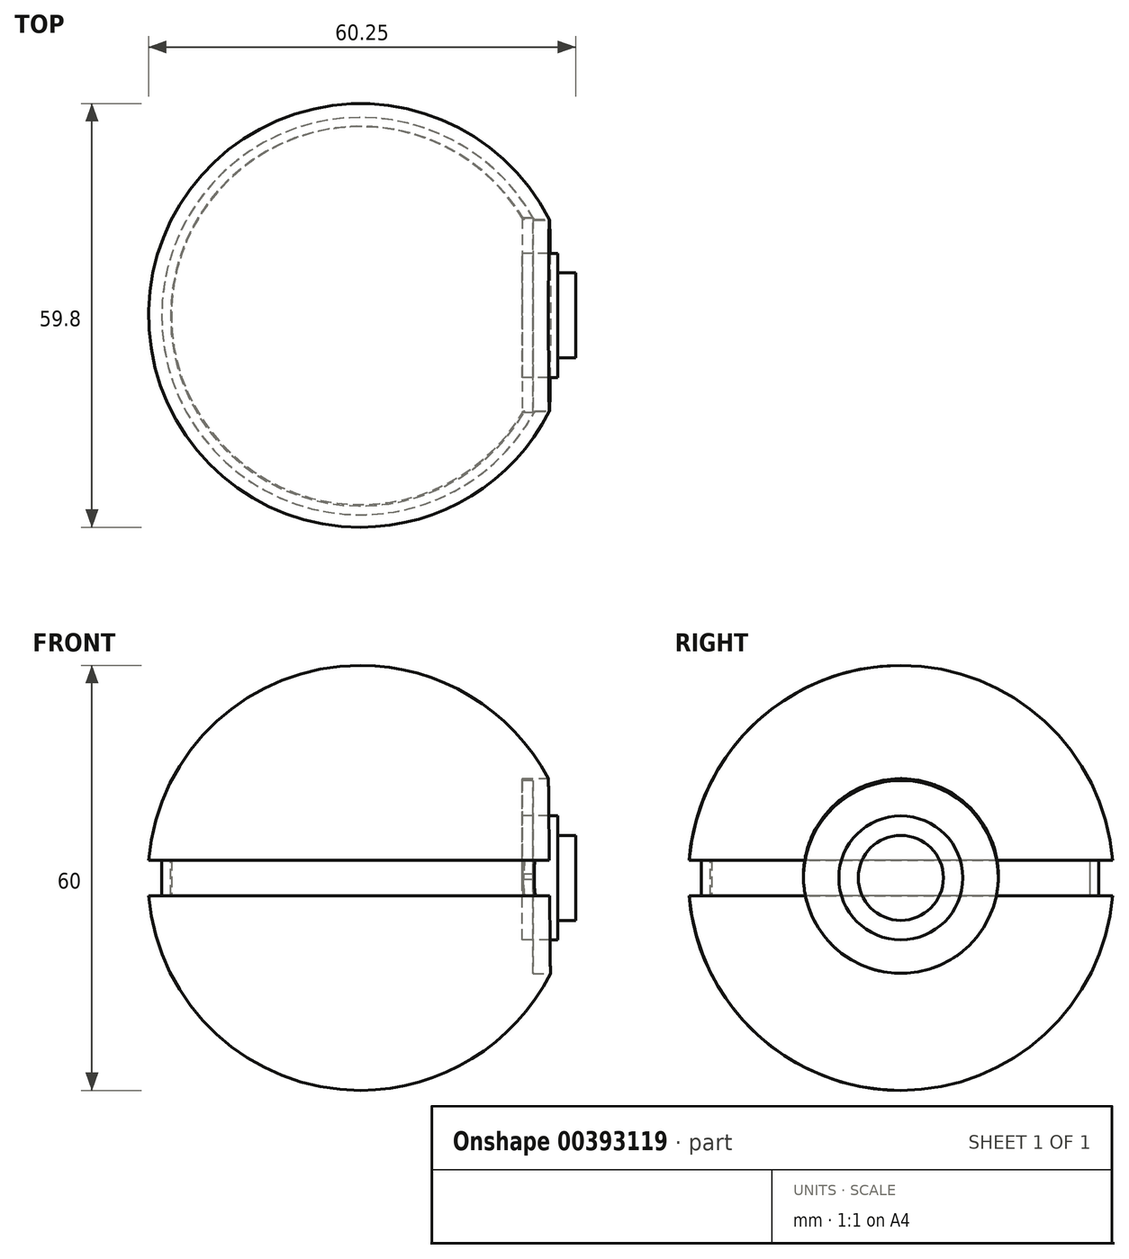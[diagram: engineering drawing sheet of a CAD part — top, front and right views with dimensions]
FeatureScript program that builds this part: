
annotation { "Feature Type Name" : "Feature", "Feature Type Description" : "" }
export const myFeature = defineFeature(function(context is Context, id is Id, definition is map)
    precondition{}
    {
        {
            var Q0;
            Q0=qCreatedBy(makeId("Right.planeOp"),FACE);
            var sketch = newSketch(context, id + "F0", { "sketchPlane" : qUnion([Q0])});
            skArc(sketch, "E0", {"start": v(0, 30) * mm, "mid": v(-21.21, 21.21) * mm, "end": v(-30, 0) * mm});
            skLineSegment(sketch, "E1", {"start": v(0, 0) * mm, "end": v(0, 30) * mm});
            skLineSegment(sketch, "E2", {"start": v(0, 0) * mm, "end": v(-30, 0) * mm});
            skSolve(sketch);
        }
        {
            var Q0;
            Q0=makeQuery(id+"F0.imprint","IMPRINT",FACE,{"disambiguationData":[TD([[makeQuery(id+"F0.imprint","IMPRINT",EDGE,{"derivedFrom":sQuery(id+"F0.wireOp",EDGE,"E0")}),1.0]])]});
            var Q1;
            Q1=sQuery(id+"F0.wireOp",EDGE,"E1");
            revolve(context, id + "F1", {"entities" : qUnion([Q0]), "axis" : qUnion([Q1]), "revolveType" : RevolveType.FULL});
        }
        {
            var Q0;
            Q0=makeQuery(id+"F1.opRevolve","SWEPT_BODY",BODY,{"disambiguationData":[OSD([sQuery(id+"F0.wireOp",EDGE,"E0"),sQuery(id+"F0.wireOp",EDGE,"E1"),sQuery(id+"F0.wireOp",EDGE,"E2")])]});
            var Q1;
            Q1=qCreatedBy(makeId("Top.planeOp"),FACE);
            mirror(context, id + "F2", {"entities" : qUnion([Q0]), "mirrorPlane" : qUnion([Q1])});
        }
        {
            var Q0;
            Q0=qCreatedBy(makeId("Right.planeOp"),FACE);
            var sketch = newSketch(context, id + "F3", { "sketchPlane" : qUnion([Q0])});
            skLineSegment(sketch, "E3.bottom", {"start": v(-34.2, 2.5) * mm, "end": v(-26.7, 2.5) * mm});
            skLineSegment(sketch, "E3.top", {"start": v(-34.2, -2.5) * mm, "end": v(-26.7, -2.5) * mm});
            skLineSegment(sketch, "E3.left", {"start": v(-34.2, 2.5) * mm, "end": v(-34.2, -2.5) * mm});
            skLineSegment(sketch, "E3.right", {"start": v(-26.7, 2.5) * mm, "end": v(-26.7, -2.5) * mm});
            skLineSegment(sketch, "E4", {"start": v(-0.03, 47.82) * mm, "end": v(-0.03, -48.43) * mm, "construction": true});
            skSolve(sketch);
        }
        {
            var Q0;
            Q0=makeQuery(id+"F3.imprint","IMPRINT",FACE,{"disambiguationData":[TD([[makeQuery(id+"F3.imprint","IMPRINT",EDGE,{"derivedFrom":sQuery(id+"F3.wireOp",EDGE,"E3.bottom")}),-1.0]])]});
            var Q1;
            Q1=sQuery(id+"F3.wireOp",EDGE,"E4");
            revolve(context, id + "F4", {"operationType" : NewBodyOperationType.REMOVE, "entities" : qUnion([Q0]), "axis" : qUnion([Q1]), "revolveType" : RevolveType.FULL, "oppositeDirection" : true});
        }
        {
            var Q0;
            Q0=qCreatedBy(makeId("Right.planeOp"),FACE);
            var sketch = newSketch(context, id + "F5", { "sketchPlane" : qUnion([Q0])});
            skLineSegment(sketch, "E5.bottom", {"start": v(-28.15, 2.5) * mm, "end": v(-26.9, 2.5) * mm});
            skLineSegment(sketch, "E5.top", {"start": v(-28.15, -2.5) * mm, "end": v(-26.9, -2.5) * mm});
            skLineSegment(sketch, "E5.left", {"start": v(-28.15, 2.5) * mm, "end": v(-28.15, -2.5) * mm});
            skLineSegment(sketch, "E5.right", {"start": v(-26.9, 2.5) * mm, "end": v(-26.9, -2.5) * mm});
            skLineSegment(sketch, "E6", {"start": v(-0.1, 32.66) * mm, "end": v(-0.1, -32.3) * mm, "construction": true});
            skSolve(sketch);
        }
        {
            var Q0;
            Q0=makeQuery(id+"F5.imprint","IMPRINT",FACE,{"disambiguationData":[TD([[makeQuery(id+"F5.imprint","IMPRINT",EDGE,{"derivedFrom":sQuery(id+"F5.wireOp",EDGE,"E5.bottom")}),-1.0]])]});
            var Q1;
            Q1=sQuery(id+"F5.wireOp",EDGE,"E6");
            revolve(context, id + "F6", {"entities" : qUnion([Q0]), "axis" : qUnion([Q1]), "revolveType" : RevolveType.FULL});
        }
        {
            var Q0;
            Q0=qCreatedBy(makeId("Right.planeOp"),FACE);
            cPlane(context, id + "F7", {"entities" : qUnion([Q0]), "cplaneType" : CPlaneType.OFFSET, "offset" : 30 * mm, "width" : 150 * mm, "height" : 150 * mm});
        }
        {
            var Q0;
            Q0=qCreatedBy(id+"F7.planeOp",FACE);
            var sketch = newSketch(context, id + "F8", { "sketchPlane" : qUnion([Q0])});
            skCircle(sketch, "E7", {"center": v(0, 0.27) * mm, "radius": 13.75 * mm});
            skSolve(sketch);
        }
        {
            var Q0;
            Q0 = qSketchRegion(id + "F8", true);
            extrude(context, id + "F9", {"entities" : qUnion([Q0]), "operationType" : NewBodyOperationType.REMOVE, "oppositeDirection" : true, "depth" : 7.15 * mm});
        }
        {
            var Q0;
            {var subQ0=makeQuery(id+"F1.opRevolve","SWEPT_FACE",FACE,{"disambiguationData":[OSD([sQuery(id+"F0.wireOp",EDGE,"E2")])]});var subQ1=sQuery(id+"F8.wireOp",EDGE,"E7");Q0=makeQuery(id+"F9.boolean.opBoolean","COPY",FACE,{"disambiguationData":[TD([subQ0])],"derivedFrom":makeQuery(id+"F9.opExtrude","CAP_FACE",FACE,{"disambiguationData":[OSD([subQ1])],"isStart":false})});}
            var sketch = newSketch(context, id + "F10", { "sketchPlane" : qUnion([Q0])});
            skCircle(sketch, "E8", {"center": v(0, 0) * mm, "radius": 13.75 * mm});
            skCircle(sketch, "E9", {"center": v(0, 0) * mm, "radius": 8.75 * mm});
            skSolve(sketch);
        }
        {
            var Q0;
            Q0 = qSketchRegion(id + "F10", true);
            extrude(context, id + "F11", {"entities" : qUnion([Q0]), "operationType" : NewBodyOperationType.ADD, "depth" : 1.5 * mm});
        }
        {
            var Q0;
            {var subQ0=makeQuery(id+"F1.opRevolve","SWEPT_FACE",FACE,{"disambiguationData":[OSD([sQuery(id+"F0.wireOp",EDGE,"E2")])]});var subQ1=sQuery(id+"F8.wireOp",EDGE,"E7");Q0=makeQuery(id+"F9.boolean.opBoolean","COPY",FACE,{"disambiguationData":[TD([subQ0])],"derivedFrom":makeQuery(id+"F9.opExtrude","CAP_FACE",FACE,{"disambiguationData":[OSD([subQ1])],"isStart":false})});}
            var sketch = newSketch(context, id + "F12", { "sketchPlane" : qUnion([Q0])});
            skCircle(sketch, "E10", {"center": v(0, 0) * mm, "radius": 8.75 * mm});
            skSolve(sketch);
        }
        {
            var Q0;
            Q0 = qSketchRegion(id + "F12", true);
            extrude(context, id + "F13", {"entities" : qUnion([Q0]), "depth" : 5 * mm});
        }
        {
            var Q0;
            Q0=makeQuery(id+"F13.opExtrude","CAP_FACE",FACE,{"disambiguationData":[OSD([sQuery(id+"F12.wireOp",EDGE,"E10")])],"isStart":false});
            var sketch = newSketch(context, id + "F14", { "sketchPlane" : qUnion([Q0])});
            skCircle(sketch, "E11", {"center": v(0, 0) * mm, "radius": 6 * mm});
            skSolve(sketch);
        }
        {
            var Q0;
            Q0 = qSketchRegion(id + "F14", true);
            extrude(context, id + "F15", {"entities" : qUnion([Q0]), "operationType" : NewBodyOperationType.ADD, "depth" : 2.5 * mm});
        }
    });
